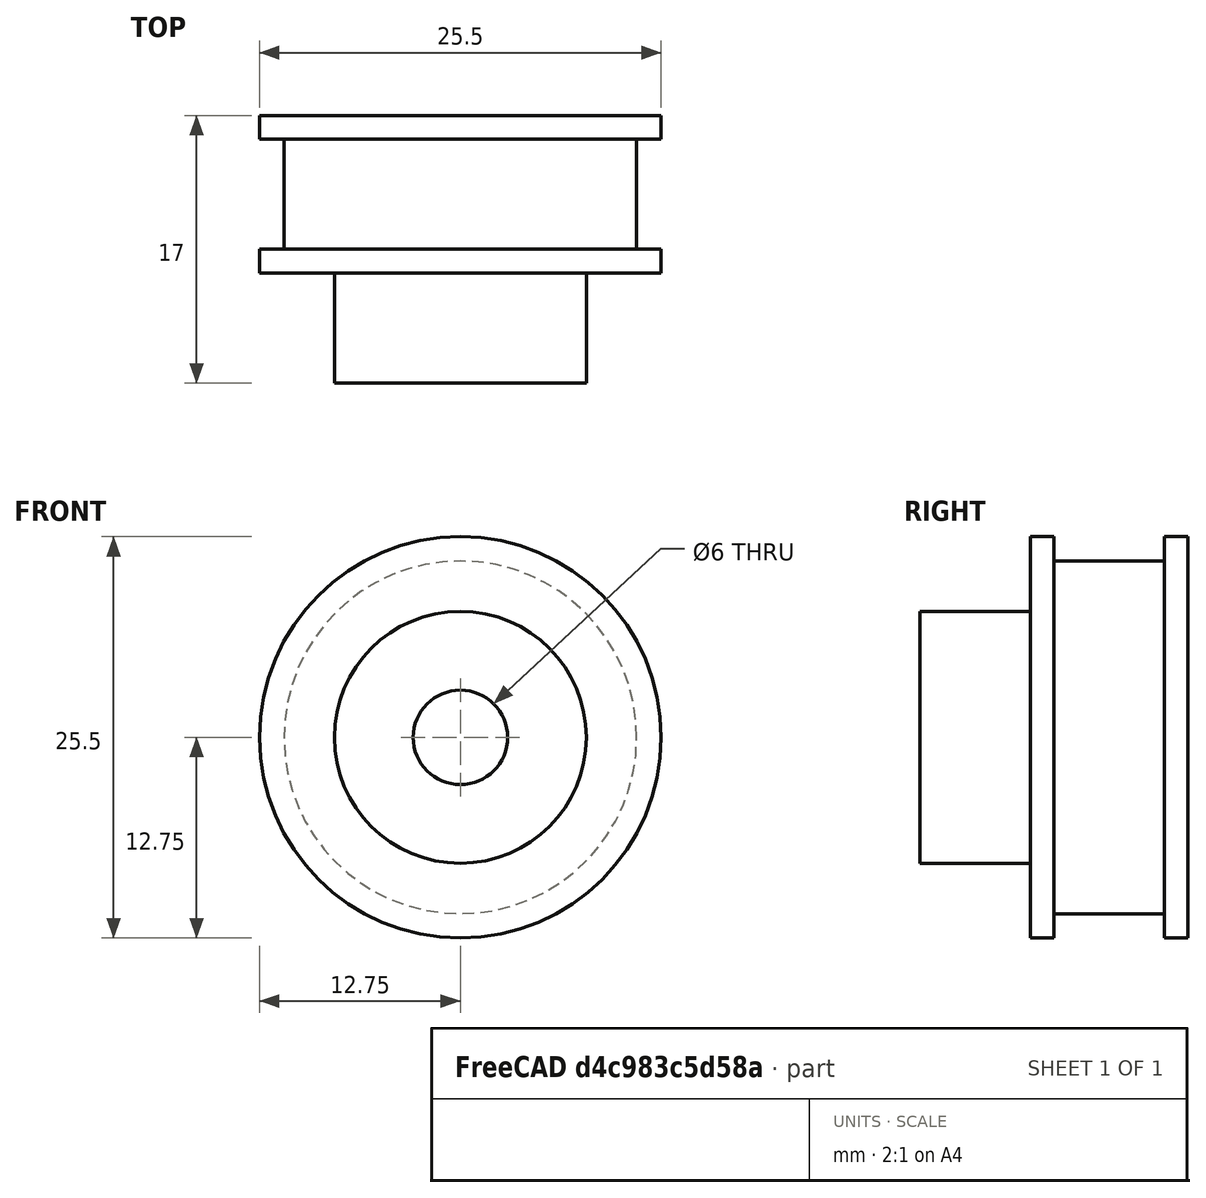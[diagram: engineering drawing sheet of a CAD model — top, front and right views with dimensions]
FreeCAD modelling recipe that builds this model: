
FCSTD DOCUMENT  (FreeCAD 0.16RUnknown)
Label: timing_pulley_gt2_36T
License: All rights reserved
LicenseURL: http://en.wikipedia.org/wiki/All_rights_reserved
objects: Sketcher::SketchObject×1, PartDesign::Revolution×1
note: 3 computed .brp shape members not serialized (recipe doc carries the construction recipe); baked Part::Feature solids carry a one-line shape summary decoded from their .brp

FEATURE [Sketcher::SketchObject] Sketch
  sketch-geometry (11):
    g0: LineSegment StartX=3 StartY=0 StartZ=0 EndX=3 EndY=17 EndZ=0
    g1: LineSegment StartX=3 StartY=17 StartZ=0 EndX=12.75 EndY=17 EndZ=0
    g2: LineSegment StartX=12.75 StartY=7 StartZ=0 EndX=8 EndY=7 EndZ=0
    g3: LineSegment StartX=8 StartY=7 StartZ=0 EndX=8 EndY=0 EndZ=0
    g4: LineSegment StartX=8 StartY=0 StartZ=0 EndX=3 EndY=0 EndZ=0
    g5: LineSegment StartX=12.75 StartY=7 StartZ=0 EndX=12.75 EndY=8.5 EndZ=0
    g6: LineSegment StartX=12.75 StartY=8.5 StartZ=0 EndX=11.2 EndY=8.5 EndZ=0
    g7: LineSegment StartX=11.2 StartY=8.5 StartZ=0 EndX=11.2 EndY=15.5 EndZ=0
    g8: LineSegment StartX=11.2 StartY=15.5 StartZ=0 EndX=12.75 EndY=15.5 EndZ=0
    g9: LineSegment StartX=12.75 StartY=15.5 StartZ=0 EndX=12.75 EndY=17 EndZ=0
    g10: LineSegment [constr] StartX=12.75 StartY=8.5 StartZ=0 EndX=12.75 EndY=15.5 EndZ=0
  constraints (32):
    c: Vertical(g0)
    c: Coincident(g0,g1)
    c: Horizontal(g1)
    c: Horizontal(g2)
    c: Coincident(g2,g3)
    c: Vertical(g3)
    c: Coincident(g3,g4)
    c: Coincident(g4,g0)
    c: Horizontal(g4)
    c: DistanceY(g0,g0) = 17
    c: PointOnObject(g0,g-1)
    c: DistanceX(g-1,g3) = 8
    c: DistanceX(g-1,g0) = 3
    c: DistanceY(g3) = -7
    c: Coincident(g5,g2)
    c: Coincident(g5,g6)
    c: Horizontal(g6)
    c: Coincident(g6,g7)
    c: Vertical(g7)
    c: Coincident(g7,g8)
    c: Horizontal(g8)
    c: Coincident(g8,g9)
    c: Coincident(g9,g1)
    c: Vertical(g9)
    c: Vertical(g5)
    c: DistanceY(g7) = 7
    c: Equal(g9,g5)
    c: Coincident(g10,g5)
    c: Coincident(g10,g8)
    c: Vertical(g10)
    c: DistanceX(g-1,g1) = 12.75
    c: DistanceX(g-1,g7) = 11.2
FEATURE [PartDesign::Revolution] Revolution
  Angle = 360
  Axis = (0,1,0)
  Base = (0,0,0)
  ReferenceAxis = -> Sketch [V_Axis]
  Reversed = true
  Sketch = -> Sketch
